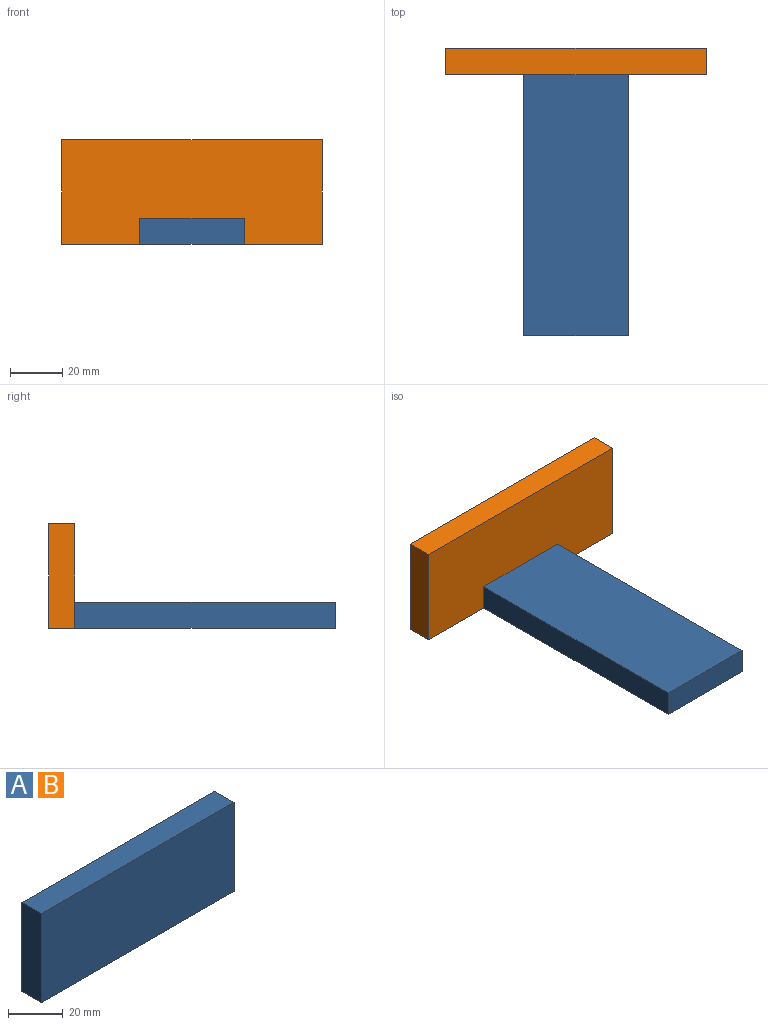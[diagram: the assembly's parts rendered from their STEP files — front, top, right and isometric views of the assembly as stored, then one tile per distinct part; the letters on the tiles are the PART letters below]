
ASSEMBLY  parts=2 mates=1
PART A: 6 faces, bbox 100x10x40 mm
  f0: plane 40x10mm, normal (1,0,0), area 400mm2, adj f1,f3,f4,f5
  f1: plane 100x10mm, normal (0,0,1), area 1000mm2, adj f0,f2,f4,f5
  f2: plane 40x10mm, normal (-1,0,0), area 400mm2, adj f1,f3,f4,f5
  f3: plane 100x10mm, normal (0,0,-1), area 1000mm2, adj f0,f2,f4,f5
  f4: plane 100x40mm, normal (0,-1,0), area 4000mm2, adj f0,f1,f2,f3
  f5: plane 100x40mm, normal (0,1,0), area 4000mm2, adj f0,f1,f2,f3
PART B: same geometry as A
PLACE A rot(axis=(-0.58,-0.58,0.58),120deg) t=(-2.93,-54.92,-17.34)mm
PLACE B t=(-2.93,5.08,2.66)mm
MATE fastened A.f0 <-> B.f4  axis (0,1,0) through (-2.93,-4.92,-17.34)mm
